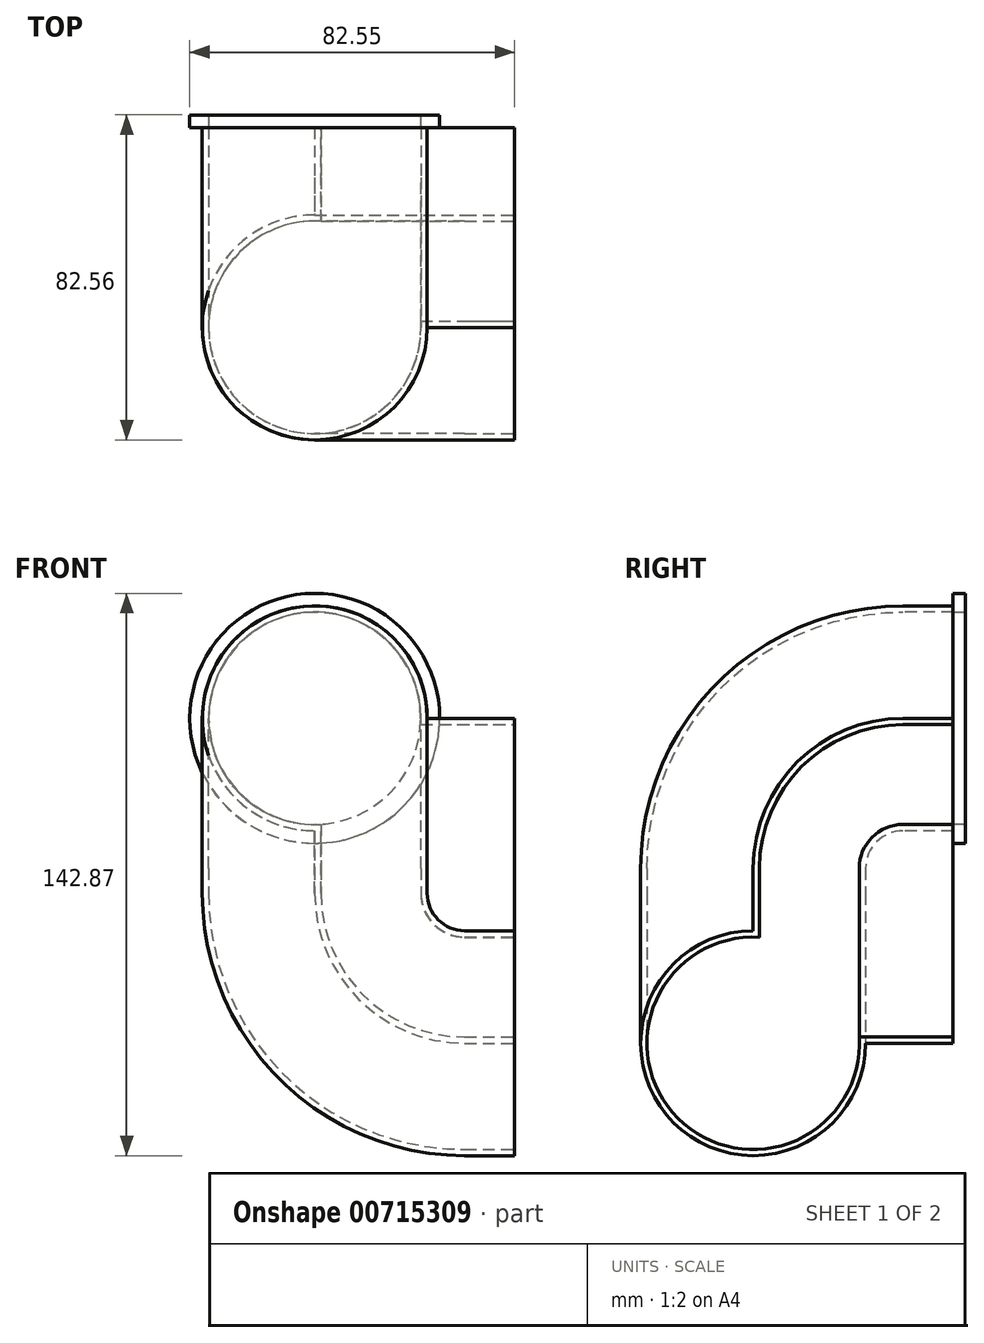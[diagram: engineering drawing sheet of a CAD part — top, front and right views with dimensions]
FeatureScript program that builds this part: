
annotation { "Feature Type Name" : "Feature", "Feature Type Description" : "" }
export const myFeature = defineFeature(function(context is Context, id is Id, definition is map)
    precondition{}
    {
        {
            var Q0;
            Q0=qCreatedBy(makeId("Top.planeOp"),FACE);
            var sketch = newSketch(context, id + "F0", { "sketchPlane" : qUnion([Q0])});
            skLineSegment(sketch, "E0.bottom", {"start": v(-25.4, 25.4) * mm, "end": v(25.4, 25.4) * mm});
            skLineSegment(sketch, "E0.top", {"start": v(-25.4, -25.4) * mm, "end": v(25.4, -25.4) * mm});
            skLineSegment(sketch, "E0.left", {"start": v(-25.4, 25.4) * mm, "end": v(-25.4, -25.4) * mm});
            skLineSegment(sketch, "E0.right", {"start": v(25.4, 25.4) * mm, "end": v(25.4, -25.4) * mm});
            skPoint(sketch, "E0.middle", {"position": v(0, 0) * mm});
            skSolve(sketch);
        }
        {
            var Q0;
            Q0 = qSketchRegion(id + "F0", true);
            extrude(context, id + "F1", {"entities" : qUnion([Q0]), "oppositeDirection" : true, "depth" : 44.45 * mm, "offsetDistance" : 25.4 * mm});
        }
        {
            var Q0;
            Q0=makeQuery(id+"F1.opExtrude","CAP_EDGE",EDGE,{"disambiguationData":[OSD([sQuery(id+"F0.wireOp",EDGE,"E0.top")])],"isStart":true});
            fillet(context, id + "F2", {"entities" : qUnion([Q0]), "radius" : 38.1 * mm, "tangentPropagation" : true, "allowEdgeOverflow" : false});
        }
        {
            var Q0;
            Q0=makeQuery(id+"F1.opExtrude","SWEPT_FACE",FACE,{"disambiguationData":[OSD([sQuery(id+"F0.wireOp",EDGE,"E0.bottom")])]});
            var sketch = newSketch(context, id + "F3", { "sketchPlane" : qUnion([Q0])});
            skCircle(sketch, "E1", {"center": v(25.4, 0) * mm, "radius": 28.58 * mm});
            skSolve(sketch);
        }
        {
            var Q0;
            {var subQ0=sQuery(id+"F3.wireOp",EDGE,"E1");var subQ1=sQuery(id+"F0.wireOp",EDGE,"E0.bottom");var subQ4=makeQuery(id+"F1.opExtrude","CAP_EDGE",EDGE,{"disambiguationData":[OSD([subQ1])],"isStart":true});var subQ5=makeQuery(id+"F3.imprint","INTERSECT",VERTEX,{"derivedFrom":[subQ4,subQ0]});Q0=makeQuery(id+"F3.imprint","IMPRINT",FACE,{"disambiguationData":[TD([[makeQuery(id+"F3.imprint","IMPRINT",EDGE,{"disambiguationData":[TD([[subQ5,1.0]])],"derivedFrom":subQ0}),1.0]])]});}
            var Q1;
            {var subQ0=sQuery(id+"F3.wireOp",EDGE,"E1");var subQ1=sQuery(id+"F0.wireOp",EDGE,"E0.bottom");var subQ4=makeQuery(id+"F1.opExtrude","CAP_EDGE",EDGE,{"disambiguationData":[OSD([subQ1])],"isStart":true});var subQ5=makeQuery(id+"F3.imprint","INTERSECT",VERTEX,{"derivedFrom":[subQ4,subQ0]});Q1=makeQuery(id+"F3.imprint","IMPRINT",FACE,{"disambiguationData":[TD([[makeQuery(id+"F3.imprint","IMPRINT",EDGE,{"disambiguationData":[TD([[subQ5,-1.0]])],"derivedFrom":subQ0}),1.0]])]});}
            var Q2;
            Q2=makeQuery(id+"F1.opExtrude","CAP_EDGE",EDGE,{"disambiguationData":[OSD([sQuery(id+"F0.wireOp",EDGE,"E0.left")])],"isStart":true});
            var Q3;
            Q3=makeQuery(id+"F2.opFillet","BLEND_EDGE",EDGE,{"blendedFrom":[makeQuery(id+"F1.opExtrude","CAP_EDGE",EDGE,{"disambiguationData":[OSD([sQuery(id+"F0.wireOp",EDGE,"E0.top")])],"isStart":true}),makeQuery(id+"F1.opExtrude","SWEPT_FACE",FACE,{"disambiguationData":[OSD([sQuery(id+"F0.wireOp",EDGE,"E0.left")])]})],"blendedInto":[makeQuery(id+"F1.opExtrude","SWEPT_FACE",FACE,{"disambiguationData":[OSD([sQuery(id+"F0.wireOp",EDGE,"E0.left")])]})]});
            var Q4;
            Q4=makeQuery(id+"F1.opExtrude","SWEPT_EDGE",EDGE,{"disambiguationData":[OSD([sQuery(id+"F0.wireOp",EDGE,"E0.top"),sQuery(id+"F0.wireOp",EDGE,"E0.left")])]});
            sweep(context, id + "F4", {"profiles" : qUnion([Q0, Q1]), "path" : qUnion([Q2, Q3, Q4])});
        }
        {
            var Q0;
            Q0=makeQuery(id+"F1.opExtrude","CAP_FACE",FACE,{"disambiguationData":[OSD([sQuery(id+"F0.wireOp",EDGE,"E0.bottom"),sQuery(id+"F0.wireOp",EDGE,"E0.top"),sQuery(id+"F0.wireOp",EDGE,"E0.left"),sQuery(id+"F0.wireOp",EDGE,"E0.right")])],"isStart":false});
            var sketch = newSketch(context, id + "F5", { "sketchPlane" : qUnion([Q0])});
            skLineSegment(sketch, "E2.bottom", {"start": v(-25.4, 25.4) * mm, "end": v(25.4, 25.4) * mm});
            skLineSegment(sketch, "E2.top", {"start": v(-25.4, -25.4) * mm, "end": v(25.4, -25.4) * mm});
            skLineSegment(sketch, "E2.left", {"start": v(-25.4, 25.4) * mm, "end": v(-25.4, -25.4) * mm});
            skLineSegment(sketch, "E2.right", {"start": v(25.4, 25.4) * mm, "end": v(25.4, -25.4) * mm});
            skPoint(sketch, "E2.middle", {"position": v(0, 0) * mm});
            skSolve(sketch);
        }
        {
            var Q0;
            Q0 = qSketchRegion(id + "F5", true);
            extrude(context, id + "F6", {"entities" : qUnion([Q0]), "depth" : 38.1 * mm, "offsetDistance" : 25.4 * mm});
        }
        {
            var Q0;
            Q0=makeQuery(id+"F6.opExtrude","CAP_EDGE",EDGE,{"disambiguationData":[OSD([sQuery(id+"F5.wireOp",EDGE,"E2.left")])],"isStart":false});
            fillet(context, id + "F7", {"entities" : qUnion([Q0]), "radius" : 38.1 * mm, "tangentPropagation" : true, "allowEdgeOverflow" : false});
        }
        {
            var Q0;
            Q0=makeQuery(id+"F4.opSweep","CAP_FACE",FACE,{"disambiguationData":[OSD([sQuery(id+"F0.wireOp",EDGE,"E0.bottom"),sQuery(id+"F0.wireOp",EDGE,"E0.top"),sQuery(id+"F0.wireOp",EDGE,"E0.left"),sQuery(id+"F3.wireOp",EDGE,"E1")])],"isStart":false});
            var Q1;
            Q1=makeQuery(id+"F6.opExtrude","SWEPT_EDGE",EDGE,{"disambiguationData":[OSD([sQuery(id+"F5.wireOp",EDGE,"E2.bottom"),sQuery(id+"F5.wireOp",EDGE,"E2.left")])]});
            var Q2;
            Q2=makeQuery(id+"F7.opFillet","BLEND_EDGE",EDGE,{"blendedFrom":[makeQuery(id+"F6.opExtrude","CAP_EDGE",EDGE,{"disambiguationData":[OSD([sQuery(id+"F5.wireOp",EDGE,"E2.left")])],"isStart":false}),makeQuery(id+"F6.opExtrude","SWEPT_FACE",FACE,{"disambiguationData":[OSD([sQuery(id+"F5.wireOp",EDGE,"E2.bottom")])]})],"blendedInto":[makeQuery(id+"F6.opExtrude","SWEPT_FACE",FACE,{"disambiguationData":[OSD([sQuery(id+"F5.wireOp",EDGE,"E2.bottom")])]})]});
            var Q3;
            Q3=makeQuery(id+"F6.opExtrude","CAP_EDGE",EDGE,{"disambiguationData":[OSD([sQuery(id+"F5.wireOp",EDGE,"E2.bottom")])],"isStart":false});
            sweep(context, id + "F8", {"operationType" : NewBodyOperationType.ADD, "profiles" : qUnion([Q0]), "path" : qUnion([Q1, Q2, Q3])});
        }
        {
            var Q0;
            Q0=makeQuery(id+"F8.opSweep","CAP_FACE",FACE,{"disambiguationData":[OSD([sQuery(id+"F0.wireOp",EDGE,"E0.bottom"),sQuery(id+"F0.wireOp",EDGE,"E0.top"),sQuery(id+"F0.wireOp",EDGE,"E0.left"),sQuery(id+"F0.wireOp",EDGE,"E0.right"),sQuery(id+"F3.wireOp",EDGE,"E1"),sQuery(id+"F5.wireOp",EDGE,"E2.bottom"),sQuery(id+"F5.wireOp",EDGE,"E2.right")])],"isStart":false});
            var Q1;
            Q1=makeQuery(id+"F4.opSweep","CAP_FACE",FACE,{"disambiguationData":[OSD([sQuery(id+"F0.wireOp",EDGE,"E0.bottom"),sQuery(id+"F0.wireOp",EDGE,"E0.left"),sQuery(id+"F3.wireOp",EDGE,"E1")])],"isStart":true});
            shell(context, id + "F9", {"entities" : qUnion([Q0, Q1]), "thickness" : 1.59 * mm});
        }
        {
            var Q0;
            Q0=makeQuery(id+"F4.opSweep","CAP_FACE",FACE,{"disambiguationData":[OSD([sQuery(id+"F0.wireOp",EDGE,"E0.bottom"),sQuery(id+"F0.wireOp",EDGE,"E0.left"),sQuery(id+"F3.wireOp",EDGE,"E1")])],"isStart":true});
            var sketch = newSketch(context, id + "F10", { "sketchPlane" : qUnion([Q0])});
            skCircle(sketch, "E3", {"center": v(25.4, 0) * mm, "radius": 31.75 * mm});
            skCircle(sketch, "E4", {"center": v(25.4, 0) * mm, "radius": 26.92 * mm});
            skSolve(sketch);
        }
        {
            var Q0;
            Q0 = qSketchRegion(id + "F10", true);
            extrude(context, id + "F11", {"entities" : qUnion([Q0]), "operationType" : NewBodyOperationType.ADD, "depth" : 3.17 * mm, "offsetDistance" : 25.4 * mm});
        }
    });
